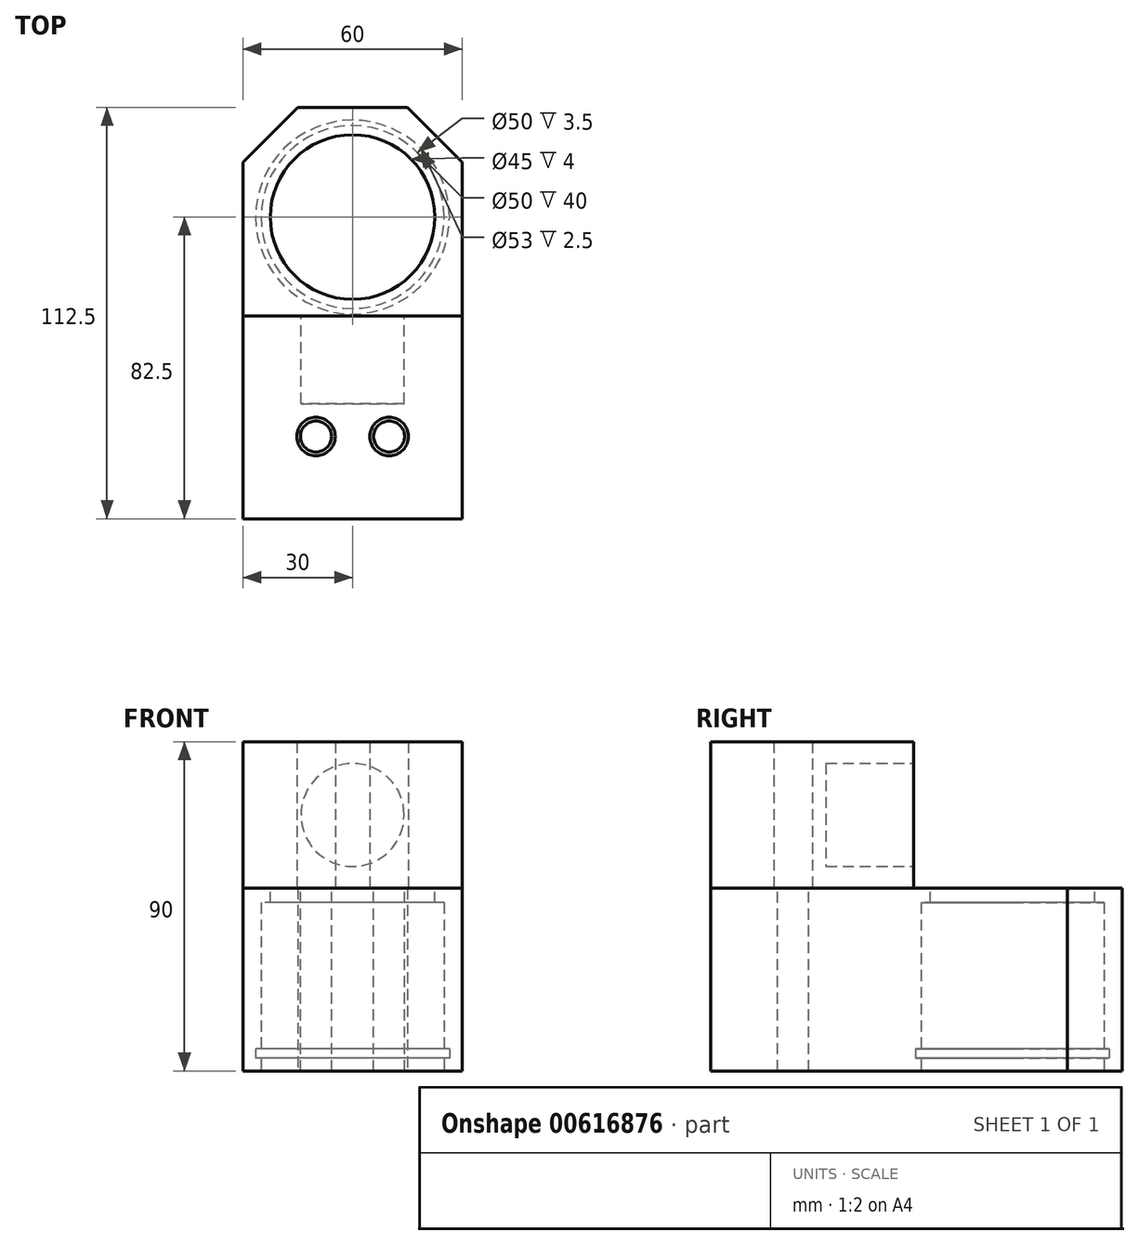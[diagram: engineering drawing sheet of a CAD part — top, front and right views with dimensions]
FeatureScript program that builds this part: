
annotation { "Feature Type Name" : "Feature", "Feature Type Description" : "" }
export const myFeature = defineFeature(function(context is Context, id is Id, definition is map)
    precondition{}
    {
        {
            var Q0;
            Q0=qCreatedBy(makeId("Top.planeOp"),FACE);
            var sketch = newSketch(context, id + "F0", { "sketchPlane" : qUnion([Q0])});
            skLineSegment(sketch, "E0.bottom", {"start": v(-15, 30) * mm, "end": v(15, 30) * mm});
            skLineSegment(sketch, "E0.top", {"start": v(-30, -82.5) * mm, "end": v(30, -82.5) * mm});
            skLineSegment(sketch, "E0.left", {"start": v(-30, 15) * mm, "end": v(-30, -82.5) * mm});
            skLineSegment(sketch, "E0.right", {"start": v(30, 15) * mm, "end": v(30, -82.5) * mm});
            skLineSegment(sketch, "E1", {"start": v(-30, 15) * mm, "end": v(-15, 30) * mm});
            skLineSegment(sketch, "E2.MirrorCS", {"start": v(30, 15) * mm, "end": v(15, 30) * mm});
            skLineSegment(sketch, "E3", {"start": v(-30, -60) * mm, "end": v(30, -60) * mm, "construction": true});
            skPoint(sketch, "E4", {"position": v(-10, -60) * mm});
            skPoint(sketch, "E5", {"position": v(10, -60) * mm});
            skPoint(sketch, "E6", {"position": v(0, 0) * mm});
            skSolve(sketch);
        }
        {
            var Q0;
            Q0 = qSketchRegion(id + "F0", true);
            extrude(context, id + "F1", {"entities" : qUnion([Q0]), "depth" : 50 * mm, "offsetDistance" : 25 * mm});
        }
        {
            var Q0;
            Q0=sQuery(id+"F0.wireOp",VERTEX,"E4");
            var Q1;
            Q1=sQuery(id+"F0.wireOp",VERTEX,"E5");
            var Q2;
            Q2=makeQuery(id+"F1.opExtrude","SWEPT_BODY",BODY,{"disambiguationData":[OSD([sQuery(id+"F0.wireOp",EDGE,"E0.bottom"),sQuery(id+"F0.wireOp",EDGE,"E0.top"),sQuery(id+"F0.wireOp",EDGE,"E0.left"),sQuery(id+"F0.wireOp",EDGE,"E0.right"),sQuery(id+"F0.wireOp",EDGE,"E1"),sQuery(id+"F0.wireOp",EDGE,"E2.MirrorCS")])]});
            hole(context, id + "F2", {"style" : HoleStyle.SIMPLE, "endStyle" : HoleEndStyle.THROUGH, "oppositeDirection" : true, "standardTappedOrClearance" : lookupTablePath({ "standard" : "ISO", "engagement" : "75%", "pitch" : "1.5 mm", "size" : "M10", "type" : "Tapped" }), "standardBlindInLast" : lookupTablePath({ "standard" : "ISO", "engagement" : "75%", "pitch" : "1.5 mm", "size" : "M10", "type" : "Tapped" }), "holeDiameter" : 8.5 * mm, "majorDiameter" : 10 * mm, "showTappedDepth" : true, "isTappedThrough" : true, "tappedDepth" : 12 * mm, "tapClearance" : 3, "locations" : qUnion([Q0, Q1]), "scope" : qUnion([Q2]), "startStyle" : HoleStartStyle.PART});
        }
        {
            var Q0;
            Q0=sQuery(id+"F0.wireOp",VERTEX,"E6");
            var Q1;
            Q1=makeQuery(id+"F1.opExtrude","SWEPT_BODY",BODY,{"disambiguationData":[OSD([sQuery(id+"F0.wireOp",EDGE,"E0.bottom"),sQuery(id+"F0.wireOp",EDGE,"E0.top"),sQuery(id+"F0.wireOp",EDGE,"E0.left"),sQuery(id+"F0.wireOp",EDGE,"E0.right"),sQuery(id+"F0.wireOp",EDGE,"E1"),sQuery(id+"F0.wireOp",EDGE,"E2.MirrorCS")])]});
            hole(context, id + "F3", {"style" : HoleStyle.SIMPLE, "endStyle" : HoleEndStyle.THROUGH, "oppositeDirection" : true, "holeDiameter" : 45 * mm, "majorDiameter" : 5 * mm, "isTappedThrough" : true, "tappedDepth" : 12 * mm, "tapClearance" : 3, "locations" : qUnion([Q0]), "scope" : qUnion([Q1]), "startStyle" : HoleStartStyle.PART});
        }
        {
            var Q0;
            Q0=qCreatedBy(makeId("Top.planeOp"),FACE);
            var sketch = newSketch(context, id + "F4", { "sketchPlane" : qUnion([Q0])});
            skCircle(sketch, "E7", {"center": v(0, 0) * mm, "radius": 25 * mm});
            skSolve(sketch);
        }
        {
            var Q0;
            Q0 = qSketchRegion(id + "F4", true);
            extrude(context, id + "F5", {"entities" : qUnion([Q0]), "operationType" : NewBodyOperationType.REMOVE, "depth" : 46 * mm, "offsetDistance" : 25 * mm});
        }
        {
            var Q0;
            Q0=qCreatedBy(makeId("Top.planeOp"),FACE);
            var sketch = newSketch(context, id + "F6", { "sketchPlane" : qUnion([Q0])});
            skCircle(sketch, "E8", {"center": v(0, 0) * mm, "radius": 26.5 * mm});
            skSolve(sketch);
        }
        {
            var Q0;
            Q0 = qSketchRegion(id + "F6", true);
            extrude(context, id + "F7", {"entities" : qUnion([Q0]), "operationType" : NewBodyOperationType.REMOVE, "depth" : 6 * mm, "offsetDistance" : 25 * mm, "hasSecondDirection" : true, "secondDirectionOppositeDirection" : false, "secondDirectionDepth" : 3.5 * mm});
        }
        {
            var Q0;
            Q0=makeQuery(id+"F1.opExtrude","CAP_FACE",FACE,{"disambiguationData":[OSD([sQuery(id+"F0.wireOp",EDGE,"E0.bottom"),sQuery(id+"F0.wireOp",EDGE,"E0.top"),sQuery(id+"F0.wireOp",EDGE,"E0.left"),sQuery(id+"F0.wireOp",EDGE,"E0.right"),sQuery(id+"F0.wireOp",EDGE,"E1"),sQuery(id+"F0.wireOp",EDGE,"E2.MirrorCS")])],"isStart":false});
            var sketch = newSketch(context, id + "F8", { "sketchPlane" : qUnion([Q0])});
            skLineSegment(sketch, "E9.0", {"start": v(-30, -82.5) * mm, "end": v(30, -82.5) * mm});
            skLineSegment(sketch, "E10.0", {"start": v(-30, 15) * mm, "end": v(-30, -82.5) * mm, "construction": true});
            skLineSegment(sketch, "E11.0", {"start": v(30, 15) * mm, "end": v(30, -82.5) * mm, "construction": true});
            skCircle(sketch, "E12.0", {"center": v(-10, -60) * mm, "radius": 4.25 * mm, "construction": true});
            skCircle(sketch, "E13.0", {"center": v(10, -60) * mm, "radius": 4.25 * mm, "construction": true});
            skLineSegment(sketch, "E14", {"start": v(-30, -27) * mm, "end": v(30, -27) * mm});
            skLineSegment(sketch, "E15", {"start": v(30, -27) * mm, "end": v(30, -82.5) * mm});
            skLineSegment(sketch, "E16", {"start": v(-30, -27) * mm, "end": v(-30, -82.5) * mm});
            skCircle(sketch, "E17.0", {"center": v(0, 0) * mm, "radius": 22.5 * mm, "construction": true});
            skCircle(sketch, "E18", {"center": v(0, 0) * mm, "radius": 15 * mm, "construction": true});
            skCircle(sketch, "E19", {"center": v(-10, -60) * mm, "radius": 5.25 * mm});
            skCircle(sketch, "E20", {"center": v(10, -60) * mm, "radius": 5.25 * mm});
            skSolve(sketch);
        }
        {
            var Q0;
            Q0 = qSketchRegion(id + "F8", true);
            extrude(context, id + "F9", {"entities" : qUnion([Q0]), "depth" : 40 * mm, "offsetDistance" : 25 * mm});
        }
        {
            var Q0;
            Q0=makeQuery(id+"F9.opExtrude","SWEPT_FACE",FACE,{"disambiguationData":[OSD([sQuery(id+"F8.wireOp",EDGE,"E14")])]});
            var sketch = newSketch(context, id + "F10", { "sketchPlane" : qUnion([Q0])});
            skLineSegment(sketch, "E21.0", {"start": v(15, 50) * mm, "end": v(-15, 50) * mm, "construction": true});
            skCircle(sketch, "E22", {"center": v(0, 70) * mm, "radius": 14.1 * mm});
            skLineSegment(sketch, "E23", {"start": v(-30, 70) * mm, "end": v(30, 70) * mm, "construction": true});
            skSolve(sketch);
        }
        {
            var Q0;
            Q0 = qSketchRegion(id + "F10", true);
            extrude(context, id + "F11", {"entities" : qUnion([Q0]), "operationType" : NewBodyOperationType.REMOVE, "oppositeDirection" : true, "depth" : 24 * mm, "offsetDistance" : 25 * mm});
        }
    });
